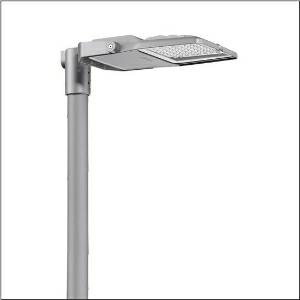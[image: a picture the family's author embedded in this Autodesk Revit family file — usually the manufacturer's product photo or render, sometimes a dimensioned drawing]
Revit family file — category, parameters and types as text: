
# Revit family: floodlight_fl_21_iq_mini___pl52_5xa7771b4d3a_0091
name_source: partatom
category: Lighting Fixtures
units: mm (PartAtom-declared; Revit-internal decimal feet)

## family parameters
Cut with Voids When Loaded = No
Host = Face
Light Source = No
Part Type = Normal
Room Calculation Point = No
Round Connector Dimension = Use Diameter
Shared = No

## types (1)
- --- (1 x LED, 6490 lm, 45.5 W, 4000K)
    Apparent Load = 46 VA
    CIE Flux Codes = 26 60 98 100 100
    Color Rendering = 70
    Color Temperature = 4000K
    Default Elevation = 1800 mm
    Description = Floodlight FL 21 iQ mini, floodlight, primary light control with lens, of PMMA, primary optical cover: protective disc, of toughened safety glass, transparent, light distribution: PL52, light emission: direct distribution, installation type: surface-mounted, lamps: LED, High Power LED, rated values: 6.490lm | 45,5W | 142,6lm/W (begin service life); end service life: 6.490lm | 48W; at 50% lumin. flux: 3.245lm | 21,5W | 150,9lm/W, colour temperature: 4000K, colour rendering: CRI > 70, light colour: 740, light setting 1 begin service life: 100% | 6.490lm | 45,5W | 142,6lm/W | 4.000K, light setting 1 end service life: 48W, further light settings possible, control: Auto-Match, Temp-Guard, Lumen-Switch, Night-Set, Smart-Wire, Light-Fading, Desk-Remote (wireless, voltage-free reading and setting of iQ features in the workshop via application-optimized NFC function/RFID function), optimised constant luminous flux control (CLO 2.0), pre-setting: linear dimming characteristic, with terminal, 6-pole, mains connection: 220..240V, AC, 50/60Hz, luminaire housing, of diecast aluminium, powder-coated, SITECO metallic grey (DB 702S), corrosivity category C5 mid according to DIN EN ISO 12944suitable for swimming poolschlorine-resistant, sealing non-destructively replaceable, please order mast flange separately, mast bracket, of steel, galvanised, powder-coated, SITECO metallic grey (DB 702S), protection rating (complete): IP66, insulation class (complete): insulation class II (safety insulation), certification: CE, ENEC, VDE, protection symbol: D, impact resistance: IK08, permissible operating ambient temperature: -40..+40°C, permissible operating ambient temperature for outdoor applications: -40..+50°C, standard: DIN EN 12944, LABS conformity tested according to VDMA 24364:2018-05, packaging unit: 1 piece

Light Distribution: PL52
    Height = 70 mm
    Lamp = 1 x LED
    Lamp Light Flux = 6490 lm
    Lamp Power = 45.5 W
    Lamp count = 1
    Length = 485 mm
    Luminous efficacy = 143 lm/W
    Manufacturer = Siteco
    ModVariant = No
    Model = 5XA7771B4D3A
    Number of Poles = 1
    OnlyDefault = Yes
    Power Factor = 1
    Product Name = Floodlight FL 21 iQ mini | PL52
    Product group = floodlight | pylon annexe
    ProductGroupID = 6201
    Protection Class = Protection class II
    Protection Degree = IP 66
    RLX_Detail_Level = 1
    RLX_Emergency_Light_Flux = 0 lm
    RLX_Emergency_Type = 0
    RLX_Emergency_Type_DB = No
    RlxData = <blob elided: 101629 chars, md5=51dbeb11>
    Socket = socket
    Standby Power = 0 W
    System Light Flux = 6490 lm
    System Power = 46 W
    Type Comments = factory setting: luminous flux: 100 % | dim-lin: 254 | 463 mA
    Type Image = l_1007125.jpg
    URL = http://relux.com
    VarID = @adj_164457
    Voltage = 0 V
    Weight = 0.00 kg
    Width = 337 mm

## geometry (parser evidence)
native form markers: Blend x4, Sweep x10
no freeform markers — native parametric forms only
